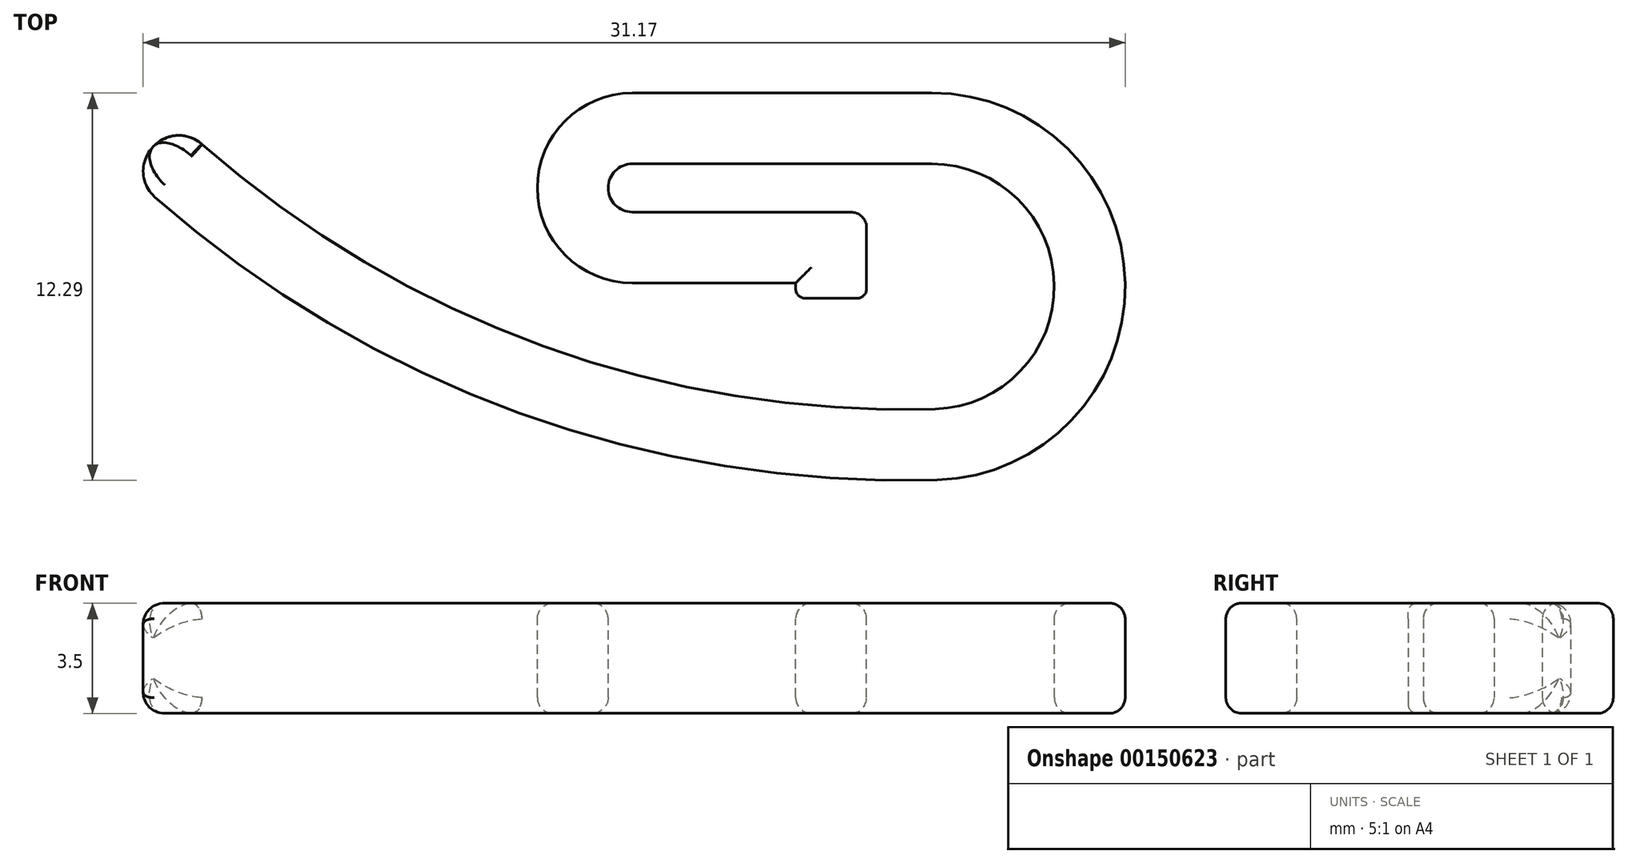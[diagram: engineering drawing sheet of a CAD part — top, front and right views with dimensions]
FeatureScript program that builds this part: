
annotation { "Feature Type Name" : "Feature", "Feature Type Description" : "" }
export const myFeature = defineFeature(function(context is Context, id is Id, definition is map)
    precondition{}
    {
        {
            var Q0;
            Q0=qCreatedBy(makeId("Top.planeOp"),FACE);
            var sketch = newSketch(context, id + "F0", { "sketchPlane" : qUnion([Q0])});
            skLineSegment(sketch, "E0", {"start": v(-21.85, 0.79) * mm, "end": v(-15.65, 0.79) * mm});
            skArc(sketch, "E1", {"start": v(-12.2, -9.46) * mm, "mid": v(-7.22, -4.26) * mm, "end": v(-12.35, 0.79) * mm});
            skArc(sketch, "E2", {"start": v(-37.15, 0) * mm, "mid": v(-25.61, -7.2) * mm, "end": v(-12.2, -9.46) * mm});
            skLineSegment(sketch, "E3", {"start": v(-21.85, -3.21) * mm, "end": v(-15.65, -3.21) * mm});
            skLineSegment(sketch, "E4", {"start": v(-15.65, -3.21) * mm, "end": v(-15.65, -4.71) * mm});
            skLineSegment(sketch, "E5", {"start": v(-15.65, -4.71) * mm, "end": v(-15.65, -3.21) * mm});
            skLineSegment(sketch, "E6", {"start": v(-15.65, 0.79) * mm, "end": v(-12.35, 0.79) * mm});
            skArc(sketch, "E7", {"start": v(-21.85, 0.79) * mm, "mid": v(-23.85, -1.21) * mm, "end": v(-21.85, -3.21) * mm});
            skSolve(sketch);
        }
        {
            var Q0;
            Q0=sQuery(id+"F0.wireOp",VERTEX,"E2.start");
            var Q1;
            Q1=sQuery(id+"F0.wireOp",EDGE,"E2");
            cPlane(context, id + "F1", {"entities" : qUnion([Q0, Q1]), "cplaneType" : CPlaneType.CURVE_POINT, "offset" : 25 * mm, "width" : 150 * mm, "height" : 150 * mm});
        }
        {
            var Q0;
            Q0=qCreatedBy(id+"F1.planeOp",FACE);
            var sketch = newSketch(context, id + "F2", { "sketchPlane" : qUnion([Q0])});
            skLineSegment(sketch, "E8.bottom", {"start": v(-26.45, 1.57) * mm, "end": v(-24.2, 1.57) * mm});
            skLineSegment(sketch, "E8.top", {"start": v(-26.45, -1.93) * mm, "end": v(-24.2, -1.93) * mm});
            skLineSegment(sketch, "E8.left", {"start": v(-26.45, 1.57) * mm, "end": v(-26.45, -1.93) * mm});
            skLineSegment(sketch, "E8.right", {"start": v(-24.2, 1.57) * mm, "end": v(-24.2, -1.93) * mm});
            skSolve(sketch);
        }
        {
            var Q0;
            Q0=makeQuery(id+"F2.imprint","IMPRINT",FACE,{"disambiguationData":[TD([[makeQuery(id+"F2.imprint","IMPRINT",EDGE,{"derivedFrom":sQuery(id+"F2.wireOp",EDGE,"E8.bottom")}),-1.0]])]});
            var Q1;
            Q1=sQuery(id+"F0.wireOp",EDGE,"E2");
            var Q2;
            Q2=sQuery(id+"F0.wireOp",EDGE,"E1");
            var Q3;
            Q3=sQuery(id+"F0.wireOp",EDGE,"E6");
            var Q4;
            Q4=sQuery(id+"F0.wireOp",EDGE,"E0");
            var Q5;
            Q5=sQuery(id+"F0.wireOp",EDGE,"E7");
            var Q6;
            Q6=sQuery(id+"F0.wireOp",EDGE,"E3");
            var Q7;
            Q7=sQuery(id+"F0.wireOp",EDGE,"E5");
            sweep(context, id + "F3", {"profiles" : qUnion([Q0]), "path" : qUnion([Q1, Q2, Q3, Q4, Q5, Q6, Q7])});
        }
        {
            var Q0;
            Q0=makeQuery(id+"F3.opSweep","SWEPT_EDGE",EDGE,{"disambiguationData":[OSD([sQuery(id+"F0.wireOp",EDGE,"E2"),sQuery(id+"F2.wireOp",EDGE,"E8.bottom"),sQuery(id+"F2.wireOp",EDGE,"E8.right")])]});
            var Q1;
            Q1=makeQuery(id+"F3.opSweep","SWEPT_EDGE",EDGE,{"disambiguationData":[OSD([sQuery(id+"F0.wireOp",EDGE,"E3"),sQuery(id+"F2.wireOp",EDGE,"E8.bottom"),sQuery(id+"F2.wireOp",EDGE,"E8.left")])]});
            var Q2;
            Q2=makeQuery(id+"F3.opSweep","SWEPT_EDGE",EDGE,{"disambiguationData":[OSD([sQuery(id+"F0.wireOp",EDGE,"E2"),sQuery(id+"F2.wireOp",EDGE,"E8.top"),sQuery(id+"F2.wireOp",EDGE,"E8.left")])]});
            var Q3;
            Q3=makeQuery(id+"F3.opSweep","SWEPT_EDGE",EDGE,{"disambiguationData":[OSD([sQuery(id+"F0.wireOp",EDGE,"E1"),sQuery(id+"F2.wireOp",EDGE,"E8.top"),sQuery(id+"F2.wireOp",EDGE,"E8.right")])]});
            var Q4;
            Q4=makeQuery(id+"F3.opSweep","SWEPT_EDGE",EDGE,{"disambiguationData":[OSD([sQuery(id+"F0.wireOp",EDGE,"E5"),sQuery(id+"F2.wireOp",EDGE,"E8.top"),sQuery(id+"F2.wireOp",EDGE,"E8.right")])]});
            var Q5;
            Q5=makeQuery(id+"F3.opSweep","SWEPT_EDGE",EDGE,{"disambiguationData":[OSD([sQuery(id+"F0.wireOp",EDGE,"E5"),sQuery(id+"F2.wireOp",EDGE,"E8.bottom"),sQuery(id+"F2.wireOp",EDGE,"E8.right")])]});
            var Q6;
            Q6=makeQuery(id+"F3.opSweep","SWEPT_EDGE",EDGE,{"disambiguationData":[OSD([sQuery(id+"F0.wireOp",EDGE,"E5"),sQuery(id+"F2.wireOp",EDGE,"E8.bottom"),sQuery(id+"F2.wireOp",EDGE,"E8.left")])]});
            var Q7;
            Q7=makeQuery(id+"F3.opSweep","MID_CAP_EDGE",EDGE,{"disambiguationData":[OSD([sQuery(id+"F0.wireOp",VERTEX,"E5.start"),sQuery(id+"F2.wireOp",EDGE,"E8.right")])],"capPos":6.0});
            var Q8;
            Q8=makeQuery(id+"F3.opSweep","SWEPT_EDGE",EDGE,{"disambiguationData":[OSD([sQuery(id+"F0.wireOp",EDGE,"E5"),sQuery(id+"F2.wireOp",EDGE,"E8.top"),sQuery(id+"F2.wireOp",EDGE,"E8.left")])]});
            fillet(context, id + "F4", {"entities" : qUnion([Q0, Q1, Q2, Q3, Q4, Q5, Q6, Q7, Q8]), "radius" : .5 * mm, "tangentPropagation" : true, "allowEdgeOverflow" : false});
        }
        {
            var Q0;
            Q0=makeQuery(id+"F3.opSweep","CAP_EDGE",EDGE,{"disambiguationData":[OSD([sQuery(id+"F0.wireOp",VERTEX,"E2.start"),sQuery(id+"F2.wireOp",EDGE,"E8.bottom")])],"isStart":true});
            var Q1;
            {var subQ0=sQuery(id+"F2.wireOp",EDGE,"E8.right");var subQ1=sQuery(id+"F2.wireOp",EDGE,"E8.bottom");Q1=makeQuery(id+"F4.opFillet","BLEND_EDGE",EDGE,{"blendedFrom":[makeQuery(id+"F3.opSweep","SWEPT_EDGE",EDGE,{"disambiguationData":[OSD([sQuery(id+"F0.wireOp",EDGE,"E2"),subQ1,subQ0])]}),makeQuery(id+"F3.opSweep","CAP_FACE",FACE,{"disambiguationData":[OSD([sQuery(id+"F0.wireOp",VERTEX,"E2.start"),subQ1,sQuery(id+"F2.wireOp",EDGE,"E8.top"),sQuery(id+"F2.wireOp",EDGE,"E8.left"),subQ0])],"isStart":true})],"blendedInto":[makeQuery(id+"F3.opSweep","CAP_FACE",FACE,{"disambiguationData":[OSD([sQuery(id+"F0.wireOp",VERTEX,"E2.start"),subQ1,sQuery(id+"F2.wireOp",EDGE,"E8.top"),sQuery(id+"F2.wireOp",EDGE,"E8.left"),subQ0])],"isStart":true})]});}
            var Q2;
            Q2=makeQuery(id+"F3.opSweep","CAP_EDGE",EDGE,{"disambiguationData":[OSD([sQuery(id+"F0.wireOp",VERTEX,"E2.start"),sQuery(id+"F2.wireOp",EDGE,"E8.right")])],"isStart":true});
            var Q3;
            {var subQ0=sQuery(id+"F2.wireOp",EDGE,"E8.right");var subQ1=sQuery(id+"F2.wireOp",EDGE,"E8.top");Q3=makeQuery(id+"F4.opFillet","BLEND_EDGE",EDGE,{"blendedFrom":[makeQuery(id+"F3.opSweep","SWEPT_EDGE",EDGE,{"disambiguationData":[OSD([sQuery(id+"F0.wireOp",EDGE,"E2"),subQ1,subQ0])]}),makeQuery(id+"F3.opSweep","CAP_FACE",FACE,{"disambiguationData":[OSD([sQuery(id+"F0.wireOp",VERTEX,"E2.start"),sQuery(id+"F2.wireOp",EDGE,"E8.bottom"),subQ1,sQuery(id+"F2.wireOp",EDGE,"E8.left"),subQ0])],"isStart":true})],"blendedInto":[makeQuery(id+"F3.opSweep","CAP_FACE",FACE,{"disambiguationData":[OSD([sQuery(id+"F0.wireOp",VERTEX,"E2.start"),sQuery(id+"F2.wireOp",EDGE,"E8.bottom"),subQ1,sQuery(id+"F2.wireOp",EDGE,"E8.left"),subQ0])],"isStart":true})]});}
            var Q4;
            Q4=makeQuery(id+"F3.opSweep","CAP_EDGE",EDGE,{"disambiguationData":[OSD([sQuery(id+"F0.wireOp",VERTEX,"E2.start"),sQuery(id+"F2.wireOp",EDGE,"E8.top")])],"isStart":true});
            var Q5;
            {var subQ0=sQuery(id+"F2.wireOp",EDGE,"E8.left");var subQ1=sQuery(id+"F2.wireOp",EDGE,"E8.top");Q5=makeQuery(id+"F4.opFillet","BLEND_EDGE",EDGE,{"blendedFrom":[makeQuery(id+"F3.opSweep","SWEPT_EDGE",EDGE,{"disambiguationData":[OSD([sQuery(id+"F0.wireOp",EDGE,"E2"),subQ1,subQ0])]}),makeQuery(id+"F3.opSweep","CAP_FACE",FACE,{"disambiguationData":[OSD([sQuery(id+"F0.wireOp",VERTEX,"E2.start"),sQuery(id+"F2.wireOp",EDGE,"E8.bottom"),subQ1,subQ0,sQuery(id+"F2.wireOp",EDGE,"E8.right")])],"isStart":true})],"blendedInto":[makeQuery(id+"F3.opSweep","CAP_FACE",FACE,{"disambiguationData":[OSD([sQuery(id+"F0.wireOp",VERTEX,"E2.start"),sQuery(id+"F2.wireOp",EDGE,"E8.bottom"),subQ1,subQ0,sQuery(id+"F2.wireOp",EDGE,"E8.right")])],"isStart":true})]});}
            var Q6;
            Q6=makeQuery(id+"F3.opSweep","CAP_EDGE",EDGE,{"disambiguationData":[OSD([sQuery(id+"F0.wireOp",VERTEX,"E2.start"),sQuery(id+"F2.wireOp",EDGE,"E8.left")])],"isStart":true});
            var Q7;
            {var subQ0=sQuery(id+"F2.wireOp",EDGE,"E8.left");var subQ1=sQuery(id+"F2.wireOp",EDGE,"E8.bottom");Q7=makeQuery(id+"F4.opFillet","BLEND_EDGE",EDGE,{"blendedFrom":[makeQuery(id+"F3.opSweep","SWEPT_EDGE",EDGE,{"disambiguationData":[OSD([sQuery(id+"F0.wireOp",EDGE,"E2"),subQ1,subQ0])]}),makeQuery(id+"F3.opSweep","CAP_FACE",FACE,{"disambiguationData":[OSD([sQuery(id+"F0.wireOp",VERTEX,"E2.start"),subQ1,sQuery(id+"F2.wireOp",EDGE,"E8.top"),subQ0,sQuery(id+"F2.wireOp",EDGE,"E8.right")])],"isStart":true})],"blendedInto":[makeQuery(id+"F3.opSweep","CAP_FACE",FACE,{"disambiguationData":[OSD([sQuery(id+"F0.wireOp",VERTEX,"E2.start"),subQ1,sQuery(id+"F2.wireOp",EDGE,"E8.top"),subQ0,sQuery(id+"F2.wireOp",EDGE,"E8.right")])],"isStart":true})]});}
            fillet(context, id + "F5", {"entities" : qUnion([Q0, Q1, Q2, Q3, Q4, Q5, Q6, Q7]), "radius" : 1.1 * mm, "tangentPropagation" : true, "allowEdgeOverflow" : false});
        }
        {
            var Q0;
            Q0=makeQuery(id+"F3.opSweep","CAP_EDGE",EDGE,{"disambiguationData":[OSD([sQuery(id+"F0.wireOp",VERTEX,"E5.end"),sQuery(id+"F2.wireOp",EDGE,"E8.top")])],"isStart":false});
            var Q1;
            Q1=makeQuery(id+"F3.opSweep","CAP_EDGE",EDGE,{"disambiguationData":[OSD([sQuery(id+"F0.wireOp",VERTEX,"E5.end"),sQuery(id+"F2.wireOp",EDGE,"E8.bottom")])],"isStart":false});
            var Q2;
            Q2=makeQuery(id+"F3.opSweep","CAP_EDGE",EDGE,{"disambiguationData":[OSD([sQuery(id+"F0.wireOp",VERTEX,"E5.end"),sQuery(id+"F2.wireOp",EDGE,"E8.right")])],"isStart":false});
            var Q3;
            Q3=makeQuery(id+"F3.opSweep","CAP_EDGE",EDGE,{"disambiguationData":[OSD([sQuery(id+"F0.wireOp",VERTEX,"E5.end"),sQuery(id+"F2.wireOp",EDGE,"E8.left")])],"isStart":false});
            fillet(context, id + "F6", {"entities" : qUnion([Q0, Q1, Q2, Q3]), "radius" : 0.3 * mm, "tangentPropagation" : true, "allowEdgeOverflow" : false});
        }
    });
